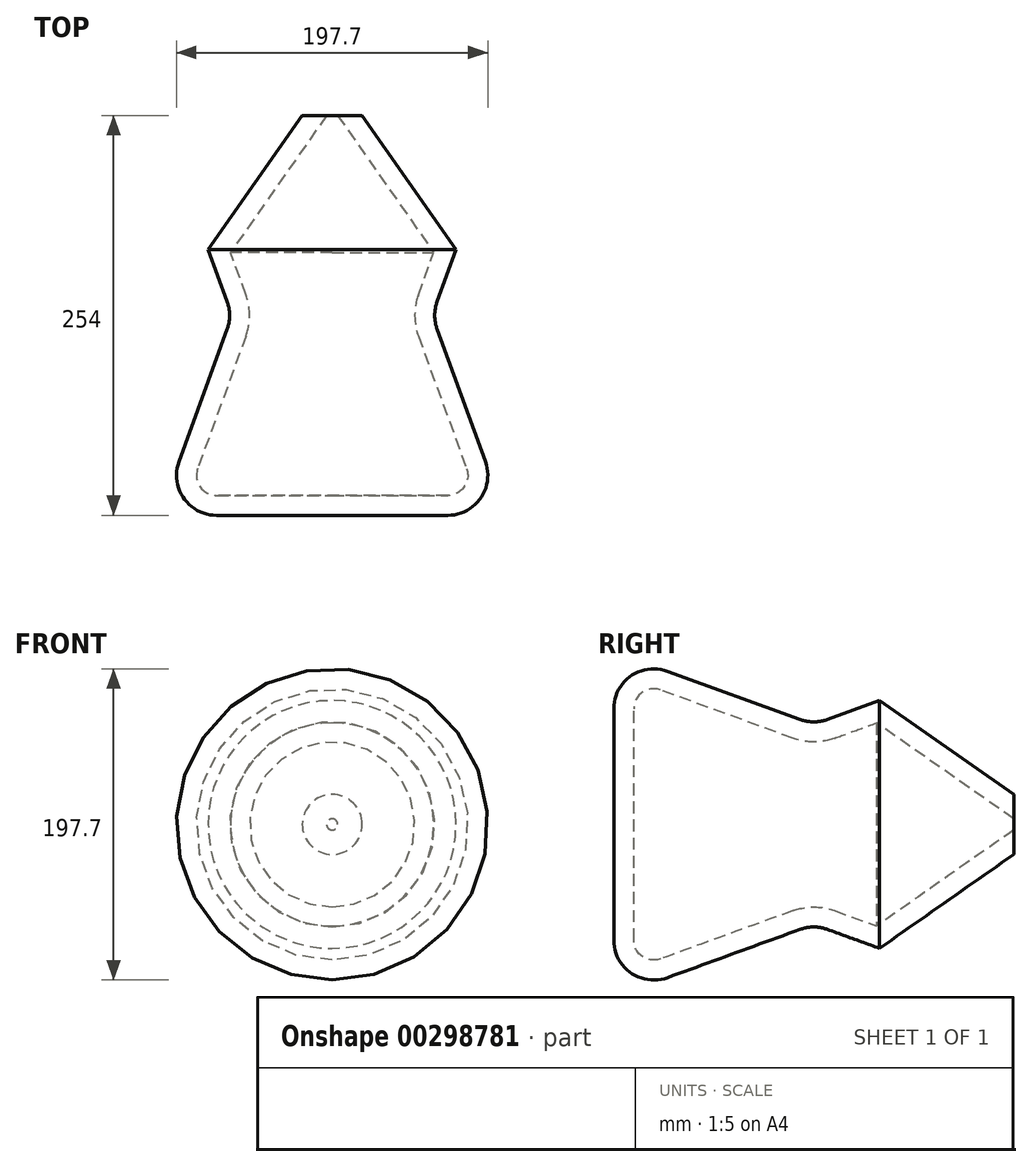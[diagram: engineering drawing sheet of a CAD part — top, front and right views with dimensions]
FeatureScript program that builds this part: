
annotation { "Feature Type Name" : "Feature", "Feature Type Description" : "" }
export const myFeature = defineFeature(function(context is Context, id is Id, definition is map)
    precondition{}
    {
        {
            var Q0;
            Q0=qCreatedBy(makeId("Front.planeOp"),FACE);
            var sketch = newSketch(context, id + "F0", { "sketchPlane" : qUnion([Q0])});
            skCircle(sketch, "E0", {"center": v(0, 0) * mm, "radius": 63.5 * mm});
            skSolve(sketch);
        }
        {
            var Q0;
            Q0=makeQuery(id+"F0.imprint","IMPRINT",FACE,{"disambiguationData":[TD([[makeQuery(id+"F0.imprint","IMPRINT",EDGE,{"derivedFrom":sQuery(id+"F0.wireOp",EDGE,"E0")}),1.0]])]});
            extrude(context, id + "F1", {"entities" : qUnion([Q0]), "endBound" : BoundingType.SYMMETRIC, "depth" : 254 * mm, "hasDraft" : true, "draftAngle" : 20 * degree});
        }
        {
            var Q0;
            {var subQ0=makeQuery(id+"F1.opExtrude","SWEPT_FACE",FACE,{"disambiguationData":[OSD([sQuery(id+"F0.wireOp",EDGE,"E0")])]});Q0=makeQuery(id+"F1.*.booleanUnion.opBoolean","MERGE",EDGE,{"derivedFrom":[makeQuery(id+"F1.*.split.splitOp","SPLIT_SURFACE_INTERSECT",EDGE,{"derivedFrom":[subQ0]}),makeQuery(id+"F1.*.split.splitOp","SPLIT_SURFACE_INTERSECT",EDGE,{"derivedFrom":[subQ0],"isFromBackBody":true})]});}
            fillet(context, id + "F2", {"entities" : qUnion([Q0]), "radius" : 25.4 * mm, "tangentPropagation" : true, "allowEdgeOverflow" : false});
        }
        {
            var Q0;
            Q0=makeQuery(id+"F1.*.split.splitOp","SPLIT",FACE,{"derivedFrom":makeQuery(id+"F1.opExtrude","SWEPT_FACE",FACE,{"disambiguationData":[OSD([sQuery(id+"F0.wireOp",EDGE,"E0")])]}),"isFromBackBody":true});
            chamfer(context, id + "F3", {"entities" : qUnion([Q0]), "width" : 63.5 * mm, "tangentPropagation" : true});
        }
        {
            var Q0;
            Q0=makeQuery(id+"F1.opExtrude","CAP_FACE",FACE,{"disambiguationData":[OSD([sQuery(id+"F0.wireOp",EDGE,"E0")])],"isStart":false});
            fillet(context, id + "F4", {"entities" : qUnion([Q0]), "radius" : 25.4 * mm, "tangentPropagation" : true, "allowEdgeOverflow" : false});
        }
        {
            var Q0;
            Q0=makeQuery(id+"F1.opExtrude","CAP_FACE",FACE,{"disambiguationData":[OSD([sQuery(id+"F0.wireOp",EDGE,"E0")])],"isStart":true});
            shell(context, id + "F5", {"entities" : qUnion([Q0]), "thickness" : 12.7 * mm});
        }
    });
